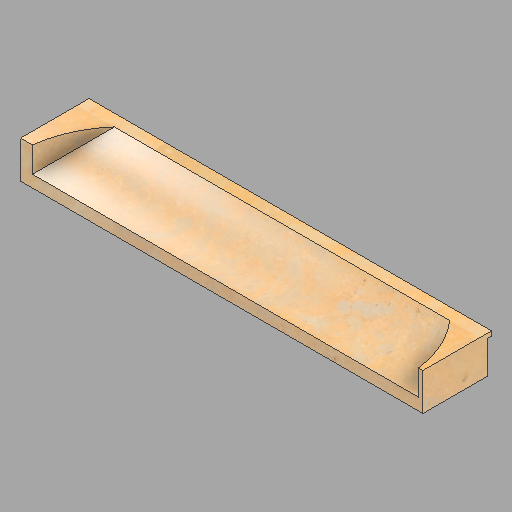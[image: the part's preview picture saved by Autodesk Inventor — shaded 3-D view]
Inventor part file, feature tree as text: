
AUTODESK INVENTOR PART (.ipt)
format: ipt  version: 2022.2 (Build 262287010, 287A)  size: 234,496 bytes
history: native  units: in
note: dims shown in document units (in); Inventor stores cm internally (conversion verified against a paired STEP export)
features: revolve x2, direct_edit x1, other x1
ambient origin geometry x8: Origin, YZ Plane, XZ Plane, XY Plane, X Axis, Y Axis, Z Axis, Center Point
bodies: Solid1 (feature_tree)
feature tree (4):
  direct_edit  "Direct Edit1"
  other  "Head (R)"
  revolve  "Rotate1"  Angle=180.0deg
  revolve  "Rotate2"  [1 undecoded]
note: 1 required parameter value undecoded (feature->parameter linkage not recoverable at this tier; creation-order binding heuristic only, values carry confidence <= 0.55)
